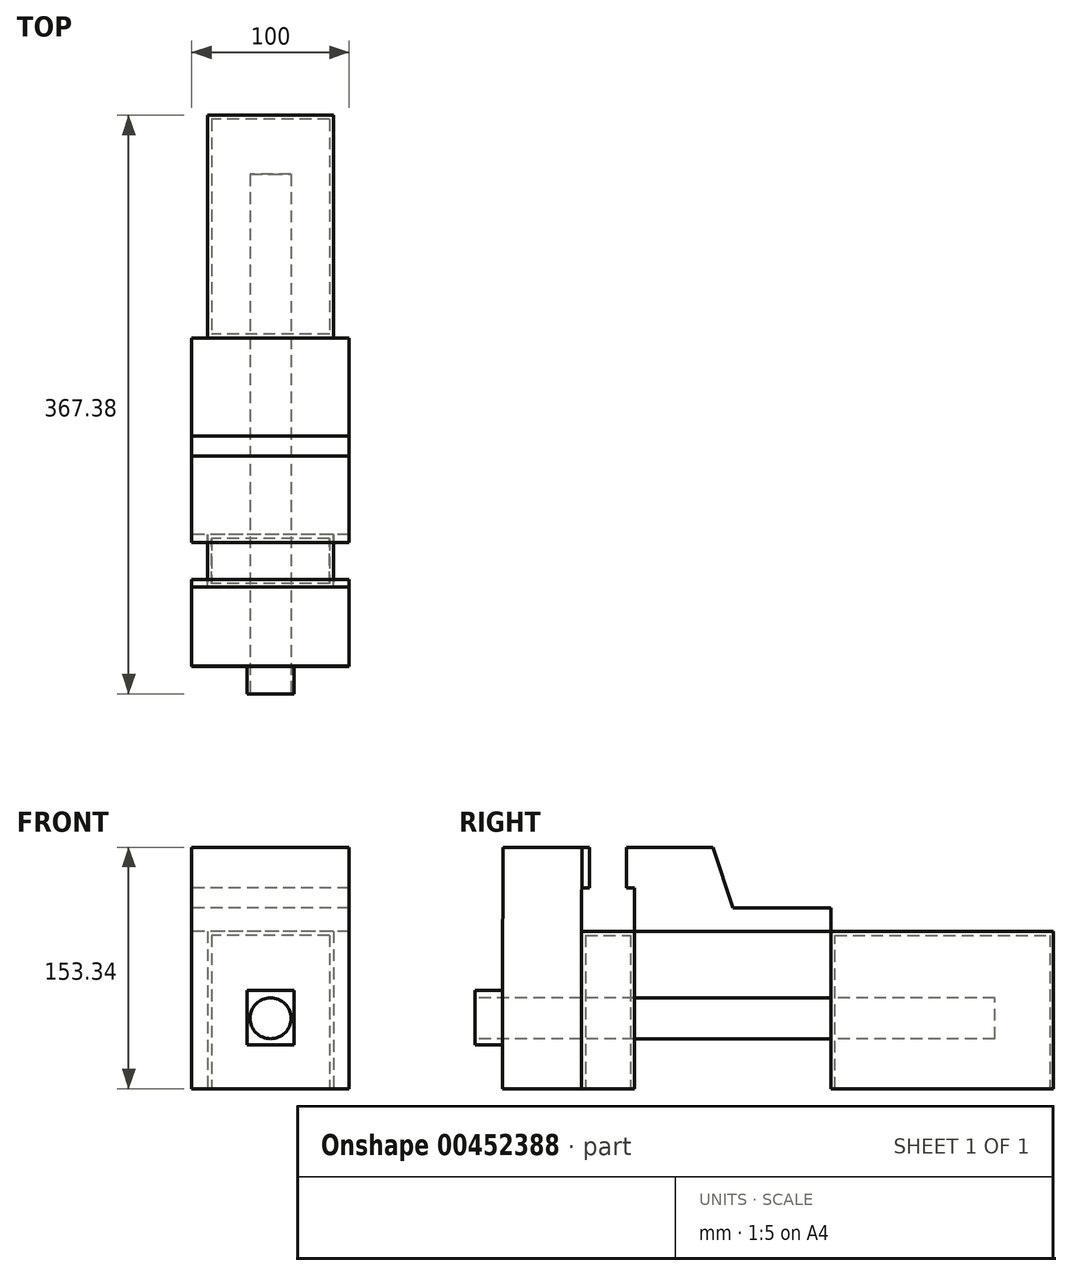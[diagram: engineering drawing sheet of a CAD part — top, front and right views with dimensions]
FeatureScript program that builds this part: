
annotation { "Feature Type Name" : "Feature", "Feature Type Description" : "" }
export const myFeature = defineFeature(function(context is Context, id is Id, definition is map)
    precondition{}
    {
        {
            var Q0;
            Q0=qCreatedBy(makeId("Right.planeOp"),FACE);
            var sketch = newSketch(context, id + "F0", { "sketchPlane" : qUnion([Q0])});
            skLineSegment(sketch, "E0", {"start": v(-53.93, -158.68) * mm, "end": v(42.5, -158.68) * mm});
            skLineSegment(sketch, "E1", {"start": v(42.5, -158.68) * mm, "end": v(42.5, -38.68) * mm});
            skLineSegment(sketch, "E2", {"start": v(42.5, -38.68) * mm, "end": v(0, -38.68) * mm});
            skLineSegment(sketch, "E3", {"start": v(0, -38.68) * mm, "end": v(-19.85, -38.68) * mm});
            skLineSegment(sketch, "E4", {"start": v(-19.85, -38.68) * mm, "end": v(-32.46, 0) * mm});
            skLineSegment(sketch, "E5", {"start": v(-32.46, 0) * mm, "end": v(-82.46, 0) * mm});
            skLineSegment(sketch, "E6", {"start": v(-82.46, 0) * mm, "end": v(-82.46, -158.68) * mm});
            skLineSegment(sketch, "E7", {"start": v(-82.46, -158.68) * mm, "end": v(-53.93, -158.68) * mm});
            skLineSegment(sketch, "E8", {"start": v(-116.15, -53.34) * mm, "end": v(183.85, -53.34) * mm});
            skLineSegment(sketch, "E9", {"start": v(183.85, -53.34) * mm, "end": v(183.85, -153.34) * mm});
            skLineSegment(sketch, "E10", {"start": v(183.85, -153.34) * mm, "end": v(-116.15, -153.34) * mm});
            skLineSegment(sketch, "E11", {"start": v(-116.15, -153.34) * mm, "end": v(-116.15, -53.34) * mm});
            skLineSegment(sketch, "E12.bottom", {"start": v(-77.46, 0) * mm, "end": v(-82.46, 0) * mm});
            skLineSegment(sketch, "E12.top", {"start": v(-74.74, -25.73) * mm, "end": v(-82.46, -25.73) * mm});
            skLineSegment(sketch, "E12.left", {"start": v(-82.46, 0) * mm, "end": v(-82.46, -25.73) * mm});
            skLineSegment(sketch, "E13.bottom", {"start": v(-165.81, 0) * mm, "end": v(-115.81, 0) * mm});
            skLineSegment(sketch, "E13.top", {"start": v(-166.15, -153.34) * mm, "end": v(-116.15, -153.34) * mm});
            skLineSegment(sketch, "E13.right", {"start": v(-115.81, 0) * mm, "end": v(-116.15, -153.34) * mm});
            skLineSegment(sketch, "E14.bottom", {"start": v(-115.81, 0) * mm, "end": v(-110.81, 0) * mm});
            skLineSegment(sketch, "E14.top", {"start": v(-115.81, -25.73) * mm, "end": v(-110.81, -25.73) * mm});
            skLineSegment(sketch, "E14.left", {"start": v(-115.81, 0) * mm, "end": v(-115.81, -25.73) * mm});
            skLineSegment(sketch, "E14.right", {"start": v(-110.81, 0) * mm, "end": v(-110.81, -25.73) * mm});
            skLineSegment(sketch, "E15.bottom", {"start": v(-82.46, -158.68) * mm, "end": v(42.5, -158.68) * mm});
            skLineSegment(sketch, "E15.top", {"start": v(-82.46, -153.34) * mm, "end": v(42.5, -153.34) * mm});
            skLineSegment(sketch, "E15.left", {"start": v(-82.46, -158.68) * mm, "end": v(-82.46, -153.34) * mm});
            skLineSegment(sketch, "E15.right", {"start": v(42.5, -158.68) * mm, "end": v(42.5, -153.34) * mm});
            skLineSegment(sketch, "E16.trimOffspring", {"start": v(-166.15, -90.97) * mm, "end": v(-166.15, -153.34) * mm});
            skLineSegment(sketch, "E17", {"start": v(-165.81, 0) * mm, "end": v(-166.15, -90.97) * mm});
            skLineSegment(sketch, "E18.bottom", {"start": v(-166.15, -90.97) * mm, "end": v(-183.53, -90.97) * mm});
            skLineSegment(sketch, "E18.top", {"start": v(-166.15, -125.4) * mm, "end": v(-183.53, -125.4) * mm});
            skLineSegment(sketch, "E18.left", {"start": v(-166.15, -90.97) * mm, "end": v(-166.15, -125.4) * mm});
            skLineSegment(sketch, "E18.right", {"start": v(-183.53, -90.97) * mm, "end": v(-183.53, -125.4) * mm});
            skLineSegment(sketch, "E19.bottom", {"start": v(-82.46, -25.73) * mm, "end": v(-87.46, -25.73) * mm});
            skLineSegment(sketch, "E19.top", {"start": v(-82.46, 0) * mm, "end": v(-87.46, 0) * mm});
            skLineSegment(sketch, "E19.left", {"start": v(-82.46, -25.73) * mm, "end": v(-82.46, 0) * mm});
            skLineSegment(sketch, "E19.right", {"start": v(-87.46, -25.73) * mm, "end": v(-87.46, 0) * mm});
            skSolve(sketch);
        }
        {
            var Q0;
            {var subQ0=sQuery(id+"F0.wireOp",EDGE,"E2");Q0=makeQuery(id+"F0.imprint","IMPRINT",FACE,{"disambiguationData":[TD([[makeQuery(id+"F0.imprint","IMPRINT",EDGE,{"derivedFrom":subQ0}),1.0]])]});}
            var Q1;
            {var subQ1=sQuery(id+"F0.wireOp",EDGE,"E11");Q1=makeQuery(id+"F0.imprint","IMPRINT",FACE,{"disambiguationData":[TD([[makeQuery(id+"F0.imprint","IMPRINT",EDGE,{"derivedFrom":subQ1}),1.0]])]});}
            var Q2;
            {var subQ0=sQuery(id+"F0.wireOp",EDGE,"E15.top");Q2=makeQuery(id+"F0.imprint","IMPRINT",FACE,{"disambiguationData":[TD([[makeQuery(id+"F0.imprint","IMPRINT",EDGE,{"derivedFrom":subQ0}),1.0]])]});}
            extrude(context, id + "F1", {"entities" : qUnion([Q0, Q1, Q2]), "endBound" : BoundingType.SYMMETRIC, "depth" : 100 * mm});
        }
        {
            var Q0;
            {var subQ5=sQuery(id+"F0.wireOp",EDGE,"E9");Q0=makeQuery(id+"F0.imprint","IMPRINT",FACE,{"disambiguationData":[TD([[makeQuery(id+"F0.imprint","IMPRINT",EDGE,{"derivedFrom":subQ5}),-1.0]])]});}
            var Q1;
            {var subQ1=sQuery(id+"F0.wireOp",EDGE,"E6");var subQ3=sQuery(id+"F0.wireOp",EDGE,"E8");var subQ4=makeQuery(id+"F0.imprint","INTERSECT",VERTEX,{"derivedFrom":[subQ1,subQ3]});Q1=makeQuery(id+"F0.imprint","IMPRINT",FACE,{"disambiguationData":[TD([[makeQuery(id+"F0.imprint","IMPRINT",EDGE,{"disambiguationData":[TD([[subQ4,1.0]])],"derivedFrom":subQ3}),-1.0]])]});}
            extrude(context, id + "F2", {"entities" : qUnion([Q0, Q1]), "operationType" : NewBodyOperationType.ADD, "endBound" : BoundingType.SYMMETRIC, "depth" : 80 * mm});
        }
        {
            var Q0;
            Q0=makeQuery(id+"F0.imprint","IMPRINT",FACE,{"disambiguationData":[TD([[makeQuery(id+"F0.imprint","IMPRINT",EDGE,{"derivedFrom":sQuery(id+"F0.wireOp",EDGE,"E14.bottom")}),-1.0]])]});
            var Q1;
            Q1=makeQuery(id+"F0.imprint","IMPRINT",FACE,{"disambiguationData":[TD([[makeQuery(id+"F0.imprint","IMPRINT",EDGE,{"derivedFrom":sQuery(id+"F0.wireOp",EDGE,"E12.bottom")}),1.0]])]});
            extrude(context, id + "F3", {"entities" : qUnion([Q0, Q1]), "operationType" : NewBodyOperationType.ADD, "endBound" : BoundingType.SYMMETRIC, "depth" : 100 * mm});
        }
        {
            var Q0;
            Q0=makeQuery(id+"F0.imprint","IMPRINT",FACE,{"disambiguationData":[TD([[makeQuery(id+"F0.imprint","IMPRINT",EDGE,{"derivedFrom":sQuery(id+"F0.wireOp",EDGE,"E19.bottom")}),-1.0]])]});
            extrude(context, id + "F4", {"entities" : qUnion([Q0]), "operationType" : NewBodyOperationType.ADD, "endBound" : BoundingType.SYMMETRIC, "depth" : 100 * mm});
        }
        {
            var Q0;
            Q0=makeQuery(id+"F0.imprint","IMPRINT",FACE,{"disambiguationData":[TD([[makeQuery(id+"F0.imprint","IMPRINT",EDGE,{"derivedFrom":sQuery(id+"F0.wireOp",EDGE,"E18.bottom")}),1.0]])]});
            extrude(context, id + "F5", {"entities" : qUnion([Q0]), "operationType" : NewBodyOperationType.ADD, "endBound" : BoundingType.SYMMETRIC, "depth" : 30 * mm});
        }
        {
            var Q0;
            {var subQ0=sQuery(id+"F0.wireOp",EDGE,"E15.top");var subQ1=sQuery(id+"F0.wireOp",EDGE,"E10");Q0=makeQuery(id+"F2.boolean.opBoolean","MERGE",FACE,{"derivedFrom":[makeQuery(id+"F1.opExtrude","SWEPT_FACE",FACE,{"disambiguationData":[OSD([subQ0])]}),makeQuery(id+"F2.opExtrude","SWEPT_FACE",FACE,{"disambiguationData":[OSD([subQ1]),TDD([makeQuery(id+"F0.imprint","IMPRINT",EDGE,{"disambiguationData":[TD([[makeQuery(id+"F0.imprint","INTERSECT",VERTEX,{"derivedFrom":[sQuery(id+"F0.wireOp",EDGE,"E9"),subQ1]}),-1.0]])],"derivedFrom":subQ1})])]}),makeQuery(id+"F2.opExtrude","SWEPT_FACE",FACE,{"disambiguationData":[OSD([subQ1]),TDD([makeQuery(id+"F0.imprint","IMPRINT",EDGE,{"disambiguationData":[TD([[makeQuery(id+"F0.imprint","INTERSECT",VERTEX,{"derivedFrom":[sQuery(id+"F0.wireOp",EDGE,"E6"),subQ1,subQ0,sQuery(id+"F0.wireOp",EDGE,"E15.left")]}),-1.0]])],"derivedFrom":subQ1})])]})]});}
            shell(context, id + "F6", {"entities" : qUnion([Q0]), "thickness" : 2.5 * mm});
        }
        {
            var Q0;
            Q0=makeQuery(id+"F5.opExtrude","SWEPT_FACE",FACE,{"disambiguationData":[OSD([sQuery(id+"F0.wireOp",EDGE,"E18.right")])]});
            var sketch = newSketch(context, id + "F7", { "sketchPlane" : qUnion([Q0])});
            skCircle(sketch, "E20", {"center": v(0, -108.6) * mm, "radius": 13 * mm});
            skSolve(sketch);
        }
        {
            var Q0;
            Q0=makeQuery(id+"F7.imprint","IMPRINT",FACE,{"disambiguationData":[TD([[makeQuery(id+"F7.imprint","IMPRINT",EDGE,{"derivedFrom":sQuery(id+"F7.wireOp",EDGE,"E20")}),1.0]])]});
            extrude(context, id + "F8", {"entities" : qUnion([Q0]), "oppositeDirection" : true, "depth" : 330 * mm});
        }
    });
